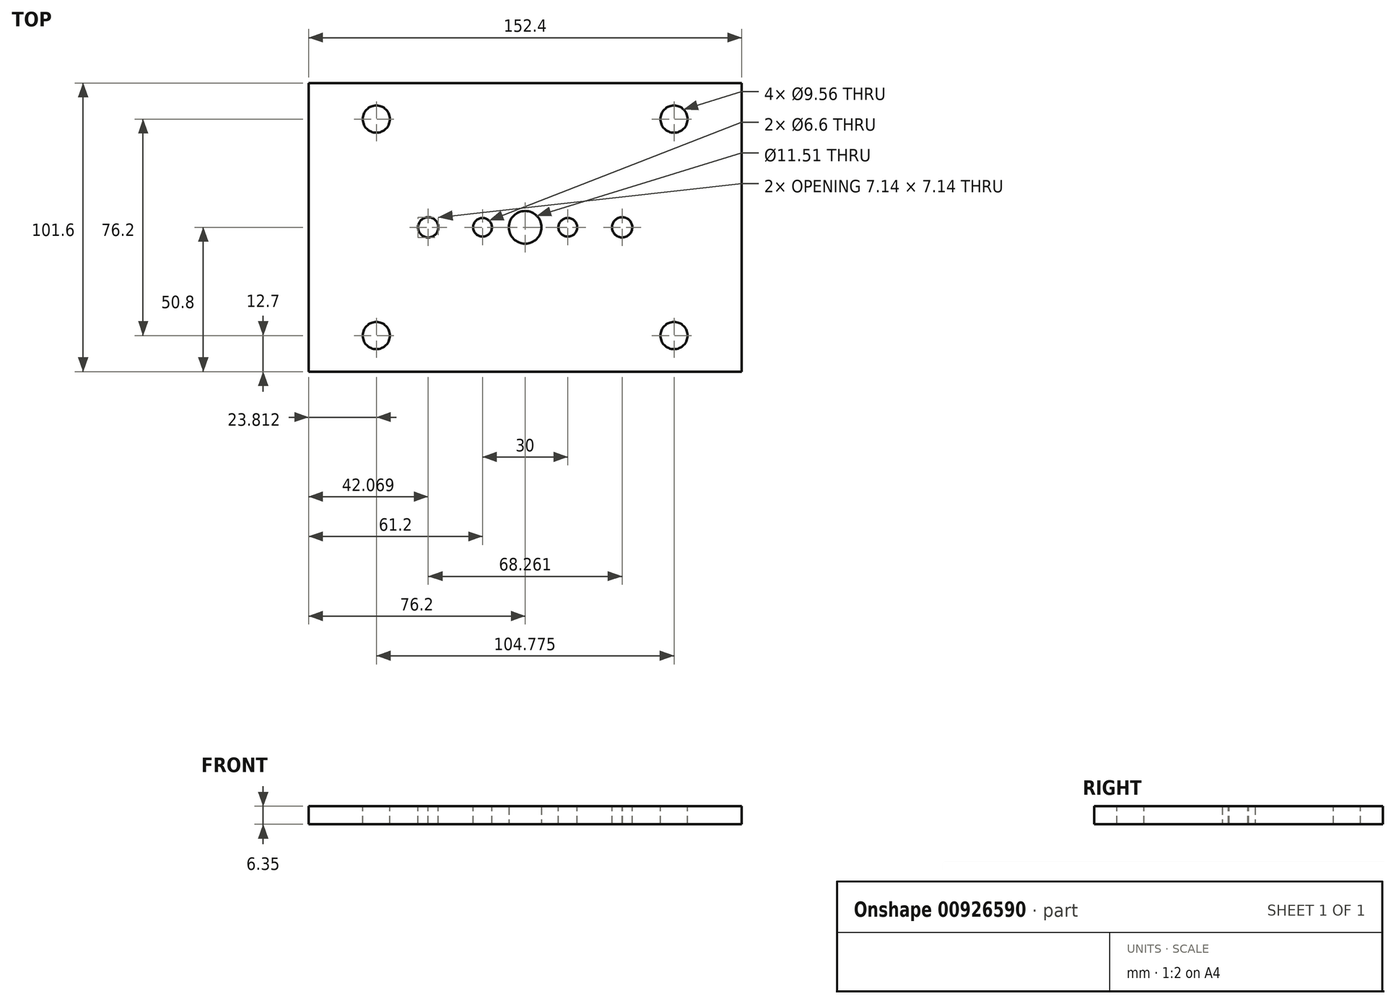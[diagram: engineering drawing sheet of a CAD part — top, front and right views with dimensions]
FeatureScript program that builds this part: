
annotation { "Feature Type Name" : "Feature", "Feature Type Description" : "" }
export const myFeature = defineFeature(function(context is Context, id is Id, definition is map)
    precondition{}
    {
        {
            var Q0;
            Q0=qCreatedBy(makeId("Top.planeOp"),FACE);
            var sketch = newSketch(context, id + "F0", { "sketchPlane" : qUnion([Q0])});
            skLineSegment(sketch, "E0.bottom", {"start": v(-76.2, 50.8) * mm, "end": v(76.2, 50.8) * mm});
            skLineSegment(sketch, "E0.top", {"start": v(-76.2, -50.8) * mm, "end": v(76.2, -50.8) * mm});
            skLineSegment(sketch, "E0.left", {"start": v(-76.2, 50.8) * mm, "end": v(-76.2, -50.8) * mm});
            skLineSegment(sketch, "E0.right", {"start": v(76.2, 50.8) * mm, "end": v(76.2, -50.8) * mm});
            skLineSegment(sketch, "E1", {"start": v(-76.2, 0) * mm, "end": v(0, 0) * mm, "construction": true});
            skLineSegment(sketch, "E2", {"start": v(0, 0) * mm, "end": v(76.2, 0) * mm, "construction": true});
            skLineSegment(sketch, "E3", {"start": v(0, 50.8) * mm, "end": v(0, 0) * mm, "construction": true});
            skLineSegment(sketch, "E4", {"start": v(0, 0) * mm, "end": v(0, -50.8) * mm, "construction": true});
            skSolve(sketch);
        }
        {
            var Q0;
            Q0=qSketchRegion(id+"F0",true);
            extrude(context, id + "F1", {"entities" : qUnion([Q0]), "depth" : 6.35 * mm, "offsetDistance" : 25.4 * mm});
        }
        {
            var Q0;
            Q0=makeQuery(id+"F1.opExtrude","CAP_FACE",FACE,{"disambiguationData":[OSD([sQuery(id+"F0.wireOp",EDGE,"E0.bottom"),sQuery(id+"F0.wireOp",EDGE,"E0.top"),sQuery(id+"F0.wireOp",EDGE,"E0.left"),sQuery(id+"F0.wireOp",EDGE,"E0.right")])],"isStart":false});
            var sketch = newSketch(context, id + "F2", { "sketchPlane" : qUnion([Q0])});
            skCircle(sketch, "E5", {"center": v(-52.39, 38.1) * mm, "radius": 4.78 * mm});
            skCircle(sketch, "E6.0.1.0", {"center": v(-52.39, -38.1) * mm, "radius": 4.78 * mm});
            skCircle(sketch, "E6.1.0.0", {"center": v(52.39, 38.1) * mm, "radius": 4.78 * mm});
            skCircle(sketch, "E6.1.1.0", {"center": v(52.39, -38.1) * mm, "radius": 4.78 * mm});
            skLineSegment(sketch, "E6.direction1", {"start": v(-52.39, 38.1) * mm, "end": v(52.39, 38.1) * mm, "construction": true});
            skLineSegment(sketch, "E6.direction2", {"start": v(-52.39, 38.1) * mm, "end": v(-52.39, -38.1) * mm, "construction": true});
            skLineSegment(sketch, "E7", {"start": v(-52.39, 38.1) * mm, "end": v(-76.2, 38.1) * mm, "construction": true});
            skLineSegment(sketch, "E8", {"start": v(52.39, 38.1) * mm, "end": v(76.2, 38.1) * mm, "construction": true});
            skLineSegment(sketch, "E9", {"start": v(-52.39, 38.1) * mm, "end": v(-52.39, 50.8) * mm, "construction": true});
            skLineSegment(sketch, "E10", {"start": v(-52.39, -38.1) * mm, "end": v(-52.39, -50.8) * mm, "construction": true});
            skSolve(sketch);
        }
        {
            var Q0;
            Q0=makeQuery(id+"F2.imprint","IMPRINT",FACE,{"disambiguationData":[TD([[makeQuery(id+"F2.imprint","IMPRINT",EDGE,{"derivedFrom":sQuery(id+"F2.wireOp",EDGE,"E5")}),1.0]])]});
            var Q1;
            Q1=makeQuery(id+"F2.imprint","IMPRINT",FACE,{"disambiguationData":[TD([[makeQuery(id+"F2.imprint","IMPRINT",EDGE,{"derivedFrom":sQuery(id+"F2.wireOp",EDGE,"E6.1.0.0")}),1.0]])]});
            var Q2;
            Q2=makeQuery(id+"F2.imprint","IMPRINT",FACE,{"disambiguationData":[TD([[makeQuery(id+"F2.imprint","IMPRINT",EDGE,{"derivedFrom":sQuery(id+"F2.wireOp",EDGE,"E6.0.1.0")}),1.0]])]});
            var Q3;
            Q3=makeQuery(id+"F2.imprint","IMPRINT",FACE,{"disambiguationData":[TD([[makeQuery(id+"F2.imprint","IMPRINT",EDGE,{"derivedFrom":sQuery(id+"F2.wireOp",EDGE,"E6.1.1.0")}),1.0]])]});
            extrude(context, id + "F3", {"entities" : qUnion([Q0, Q1, Q2, Q3]), "operationType" : NewBodyOperationType.REMOVE, "endBound" : BoundingType.UP_TO_NEXT, "oppositeDirection" : true, "depth" : 25.4 * mm, "offsetDistance" : 25.4 * mm});
        }
        {
            var Q0;
            Q0=makeQuery(id+"F1.opExtrude","CAP_FACE",FACE,{"disambiguationData":[OSD([sQuery(id+"F0.wireOp",EDGE,"E0.bottom"),sQuery(id+"F0.wireOp",EDGE,"E0.top"),sQuery(id+"F0.wireOp",EDGE,"E0.left"),sQuery(id+"F0.wireOp",EDGE,"E0.right")])],"isStart":false});
            var sketch = newSketch(context, id + "F4", { "sketchPlane" : qUnion([Q0])});
            skArc(sketch, "E11", {"start": v(-34.13, -3.57) * mm, "mid": v(-34.09, 3.57) * mm, "end": v(-34.22, -3.57) * mm});
            skArc(sketch, "E12", {"start": v(34.28, -3.57) * mm, "mid": v(34.06, 3.57) * mm, "end": v(34.13, -3.57) * mm});
            skLineSegment(sketch, "E13", {"start": v(-34.13, 0) * mm, "end": v(0, 0) * mm, "construction": true});
            skLineSegment(sketch, "E14", {"start": v(0, 0) * mm, "end": v(34.13, 0) * mm, "construction": true});
            skLineSegment(sketch, "E15", {"start": v(-34.22, -3.57) * mm, "end": v(-34.13, -3.57) * mm});
            skLineSegment(sketch, "E16", {"start": v(34.13, -3.57) * mm, "end": v(34.28, -3.57) * mm});
            skSolve(sketch);
        }
        {
            var Q0;
            Q0=makeQuery(id+"F4.imprint","IMPRINT",FACE,{"disambiguationData":[TD([[makeQuery(id+"F4.imprint","IMPRINT",EDGE,{"derivedFrom":sQuery(id+"F4.wireOp",EDGE,"E11")}),1.0]])]});
            var Q1;
            Q1=makeQuery(id+"F4.imprint","IMPRINT",FACE,{"disambiguationData":[TD([[makeQuery(id+"F4.imprint","IMPRINT",EDGE,{"derivedFrom":sQuery(id+"F4.wireOp",EDGE,"E12")}),1.0]])]});
            extrude(context, id + "F5", {"entities" : qUnion([Q0, Q1]), "operationType" : NewBodyOperationType.REMOVE, "endBound" : BoundingType.THROUGH_ALL, "oppositeDirection" : true, "depth" : 25.4 * mm, "offsetDistance" : 25.4 * mm});
        }
        {
            var Q0;
            Q0=makeQuery(id+"F1.opExtrude","CAP_FACE",FACE,{"disambiguationData":[OSD([sQuery(id+"F0.wireOp",EDGE,"E0.bottom"),sQuery(id+"F0.wireOp",EDGE,"E0.top"),sQuery(id+"F0.wireOp",EDGE,"E0.left"),sQuery(id+"F0.wireOp",EDGE,"E0.right")])],"isStart":false});
            var sketch = newSketch(context, id + "F6", { "sketchPlane" : qUnion([Q0])});
            skCircle(sketch, "E17", {"center": v(-15, 0) * mm, "radius": 3.3 * mm});
            skCircle(sketch, "E18", {"center": v(15, 0) * mm, "radius": 3.3 * mm});
            skLineSegment(sketch, "E19", {"start": v(-15, 0) * mm, "end": v(0, 0) * mm, "construction": true});
            skLineSegment(sketch, "E20", {"start": v(0, 0) * mm, "end": v(15, 0) * mm, "construction": true});
            skSolve(sketch);
        }
        {
            var Q0;
            Q0=makeQuery(id+"F6.imprint","IMPRINT",FACE,{"disambiguationData":[TD([[makeQuery(id+"F6.imprint","IMPRINT",EDGE,{"derivedFrom":sQuery(id+"F6.wireOp",EDGE,"E17")}),1.0]])]});
            var Q1;
            Q1=makeQuery(id+"F6.imprint","IMPRINT",FACE,{"disambiguationData":[TD([[makeQuery(id+"F6.imprint","IMPRINT",EDGE,{"derivedFrom":sQuery(id+"F6.wireOp",EDGE,"E18")}),1.0]])]});
            extrude(context, id + "F7", {"entities" : qUnion([Q0, Q1]), "operationType" : NewBodyOperationType.REMOVE, "endBound" : BoundingType.THROUGH_ALL, "oppositeDirection" : true, "depth" : 25.4 * mm, "offsetDistance" : 25.4 * mm});
        }
        {
            var Q0;
            Q0=makeQuery(id+"F1.opExtrude","CAP_FACE",FACE,{"disambiguationData":[OSD([sQuery(id+"F0.wireOp",EDGE,"E0.bottom"),sQuery(id+"F0.wireOp",EDGE,"E0.top"),sQuery(id+"F0.wireOp",EDGE,"E0.left"),sQuery(id+"F0.wireOp",EDGE,"E0.right")])],"isStart":true});
            var sketch = newSketch(context, id + "F8", { "sketchPlane" : qUnion([Q0])});
            skPoint(sketch, "E21", {"position": v(0, 0) * mm});
            skSolve(sketch);
        }
        {
            var Q0;
            Q0=sQuery(id+"F8.wireOp",VERTEX,"E21");
            var Q1;
            Q1=makeQuery(id+"F1.opExtrude","SWEPT_BODY",BODY,{"disambiguationData":[OSD([sQuery(id+"F0.wireOp",EDGE,"E0.bottom"),sQuery(id+"F0.wireOp",EDGE,"E0.top"),sQuery(id+"F0.wireOp",EDGE,"E0.left"),sQuery(id+"F0.wireOp",EDGE,"E0.right")])]});
            hole(context, id + "F9", {"style" : HoleStyle.SIMPLE, "endStyle" : HoleEndStyle.THROUGH, "standardTappedOrClearance" : lookupTablePath({ "standard" : "ANSI", "engagement" : "75%", "pitch" : "20 tpi", "size" : "1/2", "type" : "Tapped" }), "standardBlindInLast" : lookupTablePath({ "standard" : "ANSI", "fit" : "Normal", "engagement" : "75%", "pitch" : "20 tpi", "size" : "1/2", "type" : "Clearance & tapped" }), "holeDiameter" : 11.5 * mm, "majorDiameter" : 12.7 * mm, "showTappedDepth" : true, "isTappedThrough" : true, "tappedDepth" : 3.17 * mm, "tapClearance" : 3, "locations" : qUnion([Q0]), "scope" : qUnion([Q1])});
        }
    });
